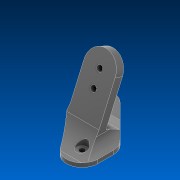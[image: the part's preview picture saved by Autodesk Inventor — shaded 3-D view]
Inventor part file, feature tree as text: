
AUTODESK INVENTOR PART (.ipt)
format: ipt  version: 2022.2 (Build 262287000, 287)  size: 239,616 bytes
history: native  units: in
note: dims shown in document units (in); Inventor stores cm internally (conversion verified against a paired STEP export)
features: sketch x4, extrude x4, other x4, projected_geometry x3, hole x2, fillet x2, plane x1, reference x1
ambient origin geometry x8: Origin, YZ Plane, XZ Plane, XY Plane, X Axis, Y Axis, Z Axis, Center Point
bodies: Solid1 (feature_tree)
feature tree (21):
  sketch  "Sketch1"  dims[d2=0.9431in d3=1.0in]
  extrude  "Extrusion1"  Depth=1.0in
  plane  "Work Plane1"
  extrude  "Extrusion2"  Depth=0.5in
  hole  "Hole2"  [1 undecoded]
  fillet  "Fillet3"  Radius=1.0in
  fillet  "Fillet2"  Radius=0.125in
  extrude  "Extrusion3"  [1 undecoded]
  hole  "Hole1"  [1 undecoded]
  extrude  "Extrusion4"  Depth=0.5in
  reference  "Reference1"
  sketch  "Sketch3"  dims[d4=0.5208in d5=0.5in]
  sketch  "Sketch4"  dims[d6=45.0deg d7=1.9074in d8=1.0in d9=0.125in d10=0.0in]
  projected_geometry  "Projected Loop1"
  projected_geometry  "Projected Loop2"
  projected_geometry  "Projected Loop3"
  sketch  "Sketch5"  dims[d11=0.175in d12=0.75in d13=0.35in d14=0.0in d15=0.5635in d16=1.0in d17=0.8108in d18=-0.8191in d20=0.4569in d21=2.1027in d22=0.25in d23=1.0in d24=0.0in d25=0.5in d26=0.8014in d27=0.175in d28=0.75in d29=0.375in d30=0.25in d31=0.5635in d32=1.0in d33=0.8108in d35=0.735in d36=0.0in d37=0.0in d38=0.319in d39=0.5in d41=0.0in d42=0.0in]
  parser-record x1  (decoder bookkeeping rows leaked as tree rows — omitted from the tree; the rows remain in map.json)
  other  "Robot.iam"
  other  "Vision Sensor (276-4850):1"
  other  "276-4850-002 Rev30_2"
note: 3 required parameter values undecoded (feature->parameter linkage not recoverable at this tier; creation-order binding heuristic only, values carry confidence <= 0.55)
note: 1 file-system path scrubbed to <path> (originals preserved in map.json)
